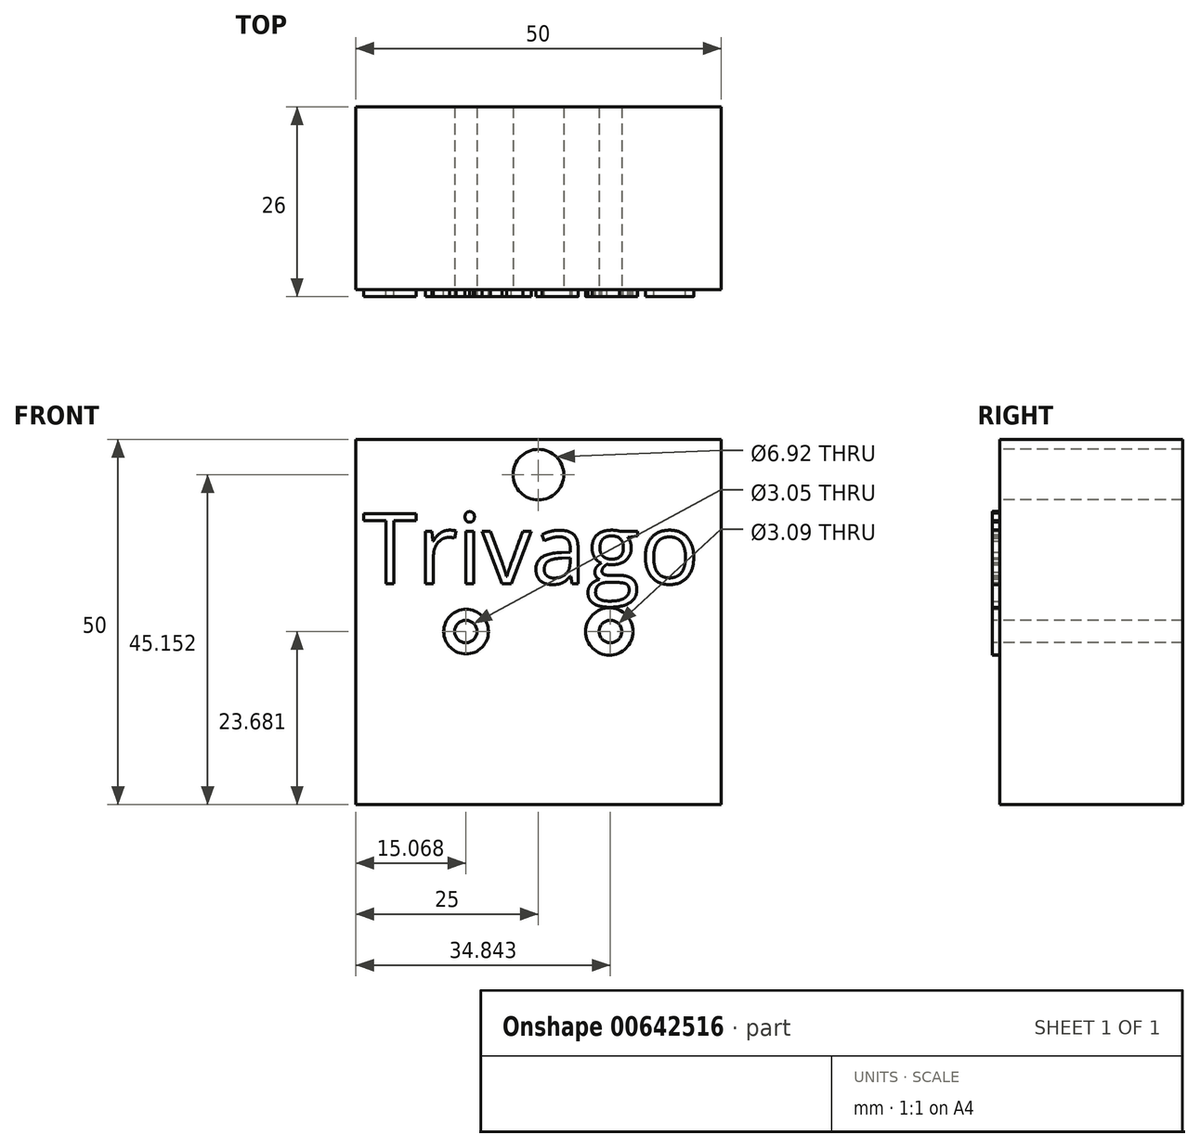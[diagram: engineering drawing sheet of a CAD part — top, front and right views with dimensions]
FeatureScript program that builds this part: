
annotation { "Feature Type Name" : "Feature", "Feature Type Description" : "" }
export const myFeature = defineFeature(function(context is Context, id is Id, definition is map)
    precondition{}
    {
        {
            var Q0;
            Q0=qCreatedBy(makeId("Front.planeOp"),FACE);
            var sketch = newSketch(context, id + "F0", { "sketchPlane" : qUnion([Q0])});
            skLineSegment(sketch, "E0.bottom", {"start": v(-25, 25) * mm, "end": v(25, 25) * mm});
            skLineSegment(sketch, "E0.top", {"start": v(-25, -25) * mm, "end": v(25, -25) * mm});
            skLineSegment(sketch, "E0.left", {"start": v(-25, 25) * mm, "end": v(-25, -25) * mm});
            skLineSegment(sketch, "E0.right", {"start": v(25, 25) * mm, "end": v(25, -25) * mm});
            skPoint(sketch, "E0.middle", {"position": v(0, 0) * mm});
            skSolve(sketch);
        }
        {
            var Q0;
            Q0=makeQuery(id+"F0.imprint","IMPRINT",FACE,{"disambiguationData":[TD([[makeQuery(id+"F0.imprint","IMPRINT",EDGE,{"derivedFrom":sQuery(id+"F0.wireOp",EDGE,"E0.bottom")}),-1.0]])]});
            extrude(context, id + "F1", {"entities" : qUnion([Q0]), "depth" : 25 * mm, "offsetDistance" : 25 * mm});
        }
        {
            var Q0;
            Q0=makeQuery(id+"F1.opExtrude","CAP_FACE",FACE,{"disambiguationData":[OSD([sQuery(id+"F0.wireOp",EDGE,"E0.bottom"),sQuery(id+"F0.wireOp",EDGE,"E0.top"),sQuery(id+"F0.wireOp",EDGE,"E0.left"),sQuery(id+"F0.wireOp",EDGE,"E0.right")])],"isStart":false});
            var sketch = newSketch(context, id + "F2", { "sketchPlane" : qUnion([Q0])});
            skCircle(sketch, "E1", {"center": v(0, 20.15) * mm, "radius": 3.46 * mm});
            skSolve(sketch);
        }
        {
            var Q0;
            Q0=makeQuery(id+"F2.imprint","IMPRINT",FACE,{"disambiguationData":[TD([[makeQuery(id+"F2.imprint","IMPRINT",EDGE,{"derivedFrom":sQuery(id+"F2.wireOp",EDGE,"E1")}),1.0]])]});
            extrude(context, id + "F3", {"entities" : qUnion([Q0]), "operationType" : NewBodyOperationType.REMOVE, "endBound" : BoundingType.UP_TO_NEXT, "oppositeDirection" : true, "depth" : 25 * mm, "offsetDistance" : 25 * mm});
        }
        {
            var Q0;
            Q0=makeQuery(id+"F1.opExtrude","CAP_FACE",FACE,{"disambiguationData":[OSD([sQuery(id+"F0.wireOp",EDGE,"E0.bottom"),sQuery(id+"F0.wireOp",EDGE,"E0.top"),sQuery(id+"F0.wireOp",EDGE,"E0.left"),sQuery(id+"F0.wireOp",EDGE,"E0.right")])],"isStart":false});
            var sketch = newSketch(context, id + "F4", { "sketchPlane" : qUnion([Q0])});
            skCircle(sketch, "E2", {"center": v(-9.93, -1.32) * mm, "radius": 1.53 * mm});
            skCircle(sketch, "E3", {"center": v(9.84, -1.32) * mm, "radius": 1.54 * mm});
            skSolve(sketch);
        }
        {
            var Q0;
            Q0=makeQuery(id+"F4.imprint","IMPRINT",FACE,{"disambiguationData":[TD([[makeQuery(id+"F4.imprint","IMPRINT",EDGE,{"derivedFrom":sQuery(id+"F4.wireOp",EDGE,"E2")}),1.0]])]});
            extrude(context, id + "F5", {"entities" : qUnion([Q0]), "operationType" : NewBodyOperationType.REMOVE, "endBound" : BoundingType.UP_TO_NEXT, "oppositeDirection" : true, "depth" : 31.4 * mm, "offsetDistance" : 25 * mm});
        }
        {
            var Q0;
            Q0=makeQuery(id+"F4.imprint","IMPRINT",FACE,{"disambiguationData":[TD([[makeQuery(id+"F4.imprint","IMPRINT",EDGE,{"derivedFrom":sQuery(id+"F4.wireOp",EDGE,"E3")}),1.0]])]});
            extrude(context, id + "F6", {"entities" : qUnion([Q0]), "operationType" : NewBodyOperationType.REMOVE, "endBound" : BoundingType.UP_TO_NEXT, "oppositeDirection" : true, "depth" : 25 * mm, "offsetDistance" : 25 * mm});
        }
        {
            var Q0;
            Q0=makeQuery(id+"F4.imprint","IMPRINT",FACE,{"disambiguationData":[TD([[makeQuery(id+"F4.imprint","IMPRINT",EDGE,{"derivedFrom":sQuery(id+"F4.wireOp",EDGE,"E2")}),-1.0]])]});
            var sketch = newSketch(context, id + "F7", { "sketchPlane" : qUnion([Q0])});
            skCircle(sketch, "E4", {"center": v(-9.9, -1.34) * mm, "radius": 3.06 * mm});
            skCircle(sketch, "E5", {"center": v(9.87, -1.42) * mm, "radius": 3.2 * mm});
            skSolve(sketch);
        }
        {
            var Q0;
            Q0=makeQuery(id+"F7.imprint","IMPRINT",FACE,{"disambiguationData":[TD([[makeQuery(id+"F7.imprint","IMPRINT",EDGE,{"derivedFrom":sQuery(id+"F7.wireOp",EDGE,"E4")}),1.0]])]});
            extrude(context, id + "F8", {"entities" : qUnion([Q0]), "operationType" : NewBodyOperationType.ADD, "depth" : 1 * mm, "offsetDistance" : 25 * mm});
        }
        {
            var Q0;
            Q0=makeQuery(id+"F4.imprint","IMPRINT",FACE,{"disambiguationData":[TD([[makeQuery(id+"F4.imprint","IMPRINT",EDGE,{"derivedFrom":sQuery(id+"F4.wireOp",EDGE,"E2")}),-1.0]])]});
            var sketch = newSketch(context, id + "F9", { "sketchPlane" : qUnion([Q0])});
            skCircle(sketch, "E6", {"center": v(9.7, -1.33) * mm, "radius": 3.23 * mm});
            skSolve(sketch);
        }
        {
            var Q0;
            Q0=makeQuery(id+"F9.imprint","IMPRINT",FACE,{"disambiguationData":[TD([[makeQuery(id+"F9.imprint","IMPRINT",EDGE,{"derivedFrom":sQuery(id+"F9.wireOp",EDGE,"E6")}),1.0]])]});
            extrude(context, id + "F10", {"entities" : qUnion([Q0]), "operationType" : NewBodyOperationType.ADD, "depth" : 1 * mm, "offsetDistance" : 25 * mm});
        }
        {
            var Q0;
            Q0=makeQuery(id+"F4.imprint","IMPRINT",FACE,{"disambiguationData":[TD([[makeQuery(id+"F4.imprint","IMPRINT",EDGE,{"derivedFrom":sQuery(id+"F4.wireOp",EDGE,"E2")}),-1.0]])]});
            var sketch = newSketch(context, id + "F11", { "sketchPlane" : qUnion([Q0])});
            skCircle(sketch, "E7", {"center": v(-9.93, -1.23) * mm, "radius": 4.7 * mm});
            skCircle(sketch, "E8", {"center": v(9.9, -1.23) * mm, "radius": 4.87 * mm});
            skSolve(sketch);
        }
        {
            var Q0;
            Q0=makeQuery(id+"F11.imprint","IMPRINT",FACE,{"disambiguationData":[TD([[makeQuery(id+"F11.imprint","IMPRINT",EDGE,{"derivedFrom":sQuery(id+"F11.wireOp",EDGE,"E7")}),-1.0]])]});
            var sketch = newSketch(context, id + "F12", { "sketchPlane" : qUnion([Q0])});
            skText(sketch, "E9", { "text": "Trivago\n", "fontName": "OpenSans-Regular.ttf"});
            const initialGuessF12  = {"E9": [-0.02403, 0.00523, 1, 0, 0.00968]};
            skSetInitialGuess(sketch, initialGuessF12);
            skSolve(sketch);
        }
        {
            var Q0;
            Q0 = qSketchRegion(id + "F12", true);
            extrude(context, id + "F13", {"entities" : qUnion([Q0]), "operationType" : NewBodyOperationType.ADD, "depth" : 1 * mm, "offsetDistance" : 25 * mm});
        }
    });
